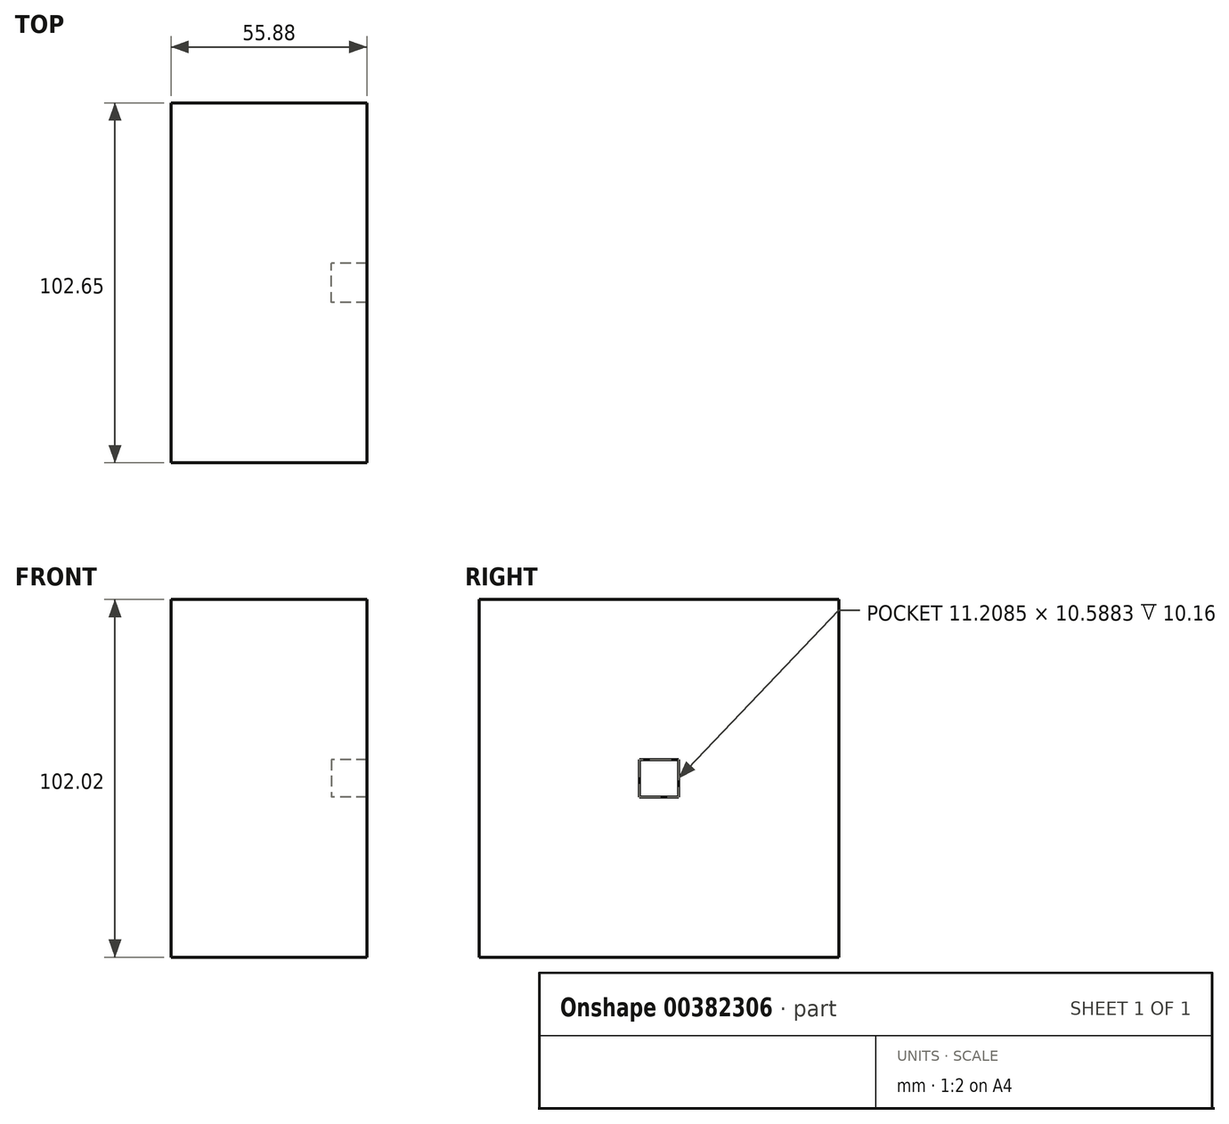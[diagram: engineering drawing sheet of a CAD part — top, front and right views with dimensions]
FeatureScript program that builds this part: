
annotation { "Feature Type Name" : "Feature", "Feature Type Description" : "" }
export const myFeature = defineFeature(function(context is Context, id is Id, definition is map)
    precondition{}
    {
        {
            var Q0;
            Q0=qCreatedBy(makeId("Right.planeOp"),FACE);
            var sketch = newSketch(context, id + "F0", { "sketchPlane" : qUnion([Q0])});
            skLineSegment(sketch, "E0.bottom", {"start": v(-59.08, 50.4) * mm, "end": v(43.57, 50.4) * mm});
            skLineSegment(sketch, "E0.top", {"start": v(-59.08, -51.63) * mm, "end": v(43.57, -51.63) * mm});
            skLineSegment(sketch, "E0.left", {"start": v(-59.08, 50.4) * mm, "end": v(-59.08, -51.63) * mm});
            skLineSegment(sketch, "E0.right", {"start": v(43.57, 50.4) * mm, "end": v(43.57, -51.63) * mm});
            skSolve(sketch);
        }
        {
            var Q0;
            Q0 = qSketchRegion(id + "F0", true);
            extrude(context, id + "F1", {"entities" : qUnion([Q0]), "depth" : 55.88 * mm, "offsetDistance" : 25.4 * mm});
        }
        {
            var Q0;
            Q0=makeQuery(id+"F1.opExtrude","CAP_FACE",FACE,{"disambiguationData":[OSD([sQuery(id+"F0.wireOp",EDGE,"E0.bottom"),sQuery(id+"F0.wireOp",EDGE,"E0.top"),sQuery(id+"F0.wireOp",EDGE,"E0.left"),sQuery(id+"F0.wireOp",EDGE,"E0.right")])],"isStart":false});
            shell(context, id + "F2", {"entities" : qUnion([Q0]), "thickness" : 45.72 * mm});
        }
    });
